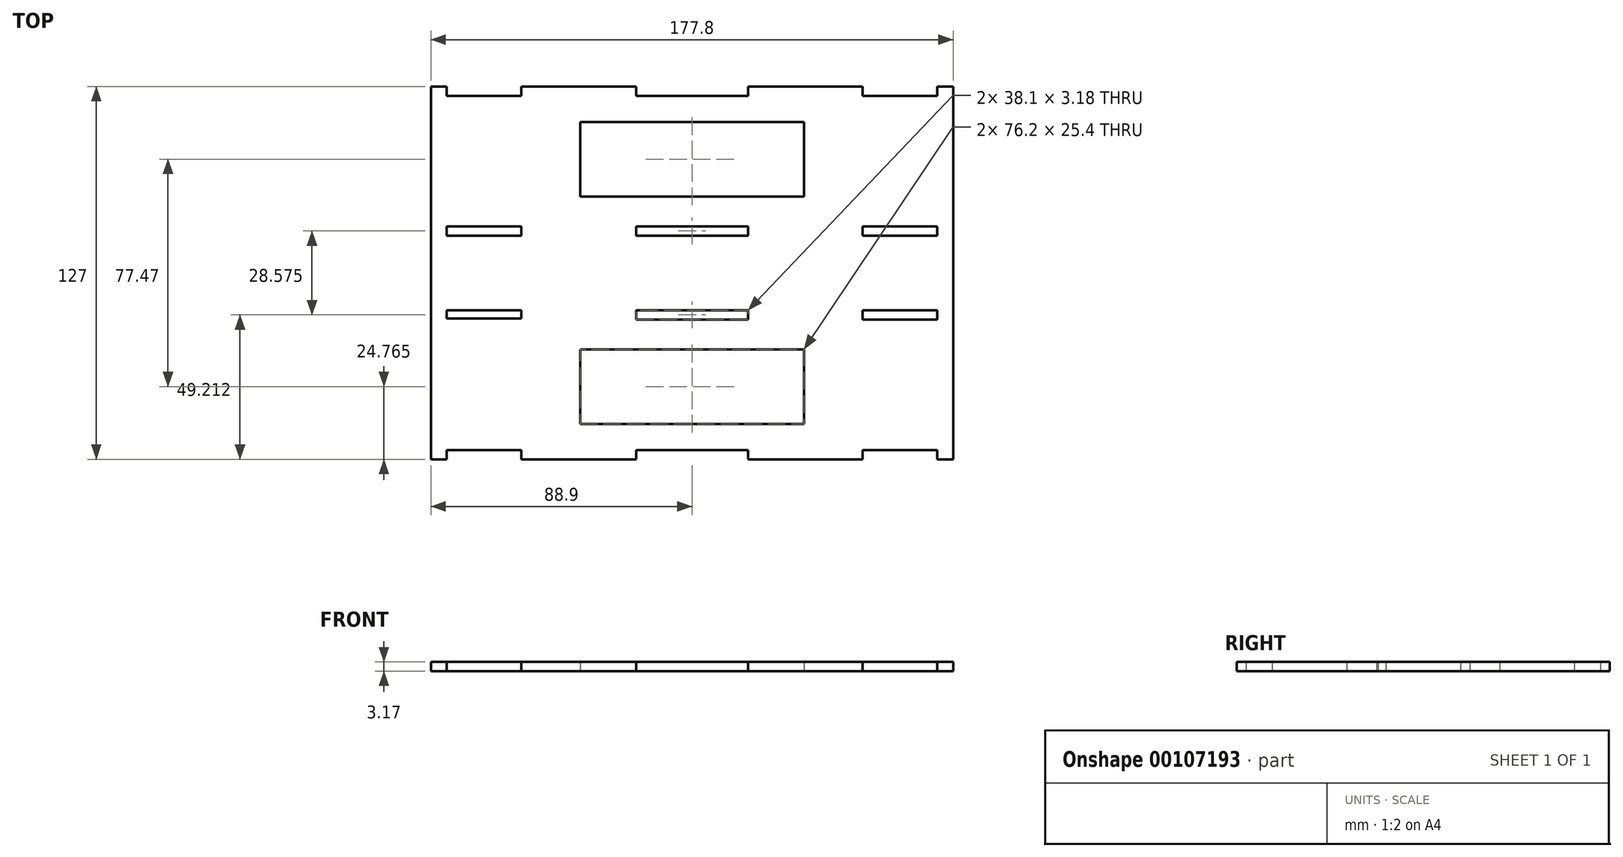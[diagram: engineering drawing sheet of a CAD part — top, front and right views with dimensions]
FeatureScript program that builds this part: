
annotation { "Feature Type Name" : "Feature", "Feature Type Description" : "" }
export const myFeature = defineFeature(function(context is Context, id is Id, definition is map)
    precondition{}
    {
        {
            var Q0;
            Q0=qCreatedBy(makeId("Top.planeOp"),FACE);
            var sketch = newSketch(context, id + "F0", { "sketchPlane" : qUnion([Q0])});
            skPoint(sketch, "E0.middle", {"position": v(0, 0) * mm});
            skPoint(sketch, "E1", {"position": v(-76.2, 0) * mm});
            skPoint(sketch, "E2", {"position": v(101.6, 0) * mm});
            skLineSegment(sketch, "E3", {"start": v(-76.2, 63.5) * mm, "end": v(-76.2, -63.5) * mm});
            skLineSegment(sketch, "E4.bottom", {"start": v(-76.2, 63.5) * mm, "end": v(-70.75, 63.5) * mm});
            skLineSegment(sketch, "E4.right", {"start": v(101.6, 63.5) * mm, "end": v(101.6, -63.5) * mm});
            skPoint(sketch, "E5", {"position": v(12.7, 76.2) * mm});
            skPoint(sketch, "E6", {"position": v(12.7, 63.5) * mm});
            skLineSegment(sketch, "E7.MirrorCS", {"start": v(70.75, 63.5) * mm, "end": v(70.75, 60.32) * mm});
            skLineSegment(sketch, "E8.MirrorCS", {"start": v(31.75, 60.32) * mm, "end": v(-6.35, 60.32) * mm});
            skLineSegment(sketch, "E9.MirrorCS", {"start": v(-70.75, 60.32) * mm, "end": v(-45.35, 60.32) * mm});
            skLineSegment(sketch, "E10.MirrorCS", {"start": v(-6.35, 63.5) * mm, "end": v(-6.35, 60.32) * mm});
            skLineSegment(sketch, "E11.MirrorCS", {"start": v(-70.75, 63.5) * mm, "end": v(-70.75, 60.32) * mm});
            skLineSegment(sketch, "E12.MirrorCS", {"start": v(96.15, 63.5) * mm, "end": v(96.15, 60.32) * mm});
            skLineSegment(sketch, "E13.MirrorCS", {"start": v(96.15, 60.32) * mm, "end": v(70.75, 60.32) * mm});
            skLineSegment(sketch, "E14.MirrorCS", {"start": v(31.75, 63.5) * mm, "end": v(31.75, 60.32) * mm});
            skLineSegment(sketch, "E15.MirrorCS", {"start": v(-45.35, 63.5) * mm, "end": v(-45.35, 60.32) * mm});
            skLineSegment(sketch, "E16.trimOffspring", {"start": v(-45.35, 63.5) * mm, "end": v(-6.35, 63.5) * mm});
            skLineSegment(sketch, "E17.trimOffspring", {"start": v(31.75, 63.5) * mm, "end": v(70.75, 63.5) * mm});
            skLineSegment(sketch, "E18.trimOffspring", {"start": v(96.15, 63.5) * mm, "end": v(101.6, 63.5) * mm});
            skPoint(sketch, "E19", {"position": v(90.87, -11.07) * mm});
            skLineSegment(sketch, "E20.MirrorCS", {"start": v(70.75, -12.7) * mm, "end": v(70.75, -15.88) * mm});
            skLineSegment(sketch, "E21.MirrorCS", {"start": v(31.75, -15.88) * mm, "end": v(-6.35, -15.88) * mm});
            skLineSegment(sketch, "E22.MirrorCS", {"start": v(-70.75, -12.7) * mm, "end": v(-45.35, -12.7) * mm});
            skLineSegment(sketch, "E23.MirrorCS", {"start": v(-6.35, -12.7) * mm, "end": v(-6.35, -15.88) * mm});
            skLineSegment(sketch, "E24.MirrorCS", {"start": v(-70.75, -12.7) * mm, "end": v(-70.75, -15.47) * mm});
            skLineSegment(sketch, "E25.MirrorCS", {"start": v(96.15, -12.7) * mm, "end": v(96.15, -15.88) * mm});
            skLineSegment(sketch, "E26.MirrorCS", {"start": v(96.15, -15.88) * mm, "end": v(70.75, -15.88) * mm});
            skLineSegment(sketch, "E27.MirrorCS", {"start": v(31.75, -12.7) * mm, "end": v(31.75, -15.88) * mm});
            skLineSegment(sketch, "E28.MirrorCS", {"start": v(-45.35, -12.7) * mm, "end": v(-45.35, -15.47) * mm});
            skLineSegment(sketch, "E29", {"start": v(96.15, -12.7) * mm, "end": v(70.75, -12.7) * mm});
            skLineSegment(sketch, "E30", {"start": v(31.75, -12.7) * mm, "end": v(-6.35, -12.7) * mm});
            skLineSegment(sketch, "E31", {"start": v(-45.35, -15.47) * mm, "end": v(-70.75, -15.47) * mm});
            skLineSegment(sketch, "E32.MirrorCS", {"start": v(96.15, 12.7) * mm, "end": v(96.15, 15.87) * mm});
            skLineSegment(sketch, "E33.MirrorCS", {"start": v(70.75, 12.7) * mm, "end": v(70.75, 15.87) * mm});
            skLineSegment(sketch, "E34.MirrorCS", {"start": v(-6.35, 12.7) * mm, "end": v(-6.35, 15.87) * mm});
            skLineSegment(sketch, "E35.MirrorCS", {"start": v(-70.75, 12.7) * mm, "end": v(-70.75, 15.87) * mm});
            skLineSegment(sketch, "E36.MirrorCS", {"start": v(-45.35, 12.7) * mm, "end": v(-45.35, 15.87) * mm});
            skLineSegment(sketch, "E37.MirrorCS", {"start": v(31.75, 12.7) * mm, "end": v(31.75, 15.87) * mm});
            skLineSegment(sketch, "E38.MirrorCS", {"start": v(-70.75, 15.87) * mm, "end": v(-45.35, 15.87) * mm});
            skLineSegment(sketch, "E39.MirrorCS", {"start": v(31.75, 15.87) * mm, "end": v(-6.35, 15.87) * mm});
            skLineSegment(sketch, "E40.MirrorCS", {"start": v(96.15, 12.7) * mm, "end": v(70.75, 12.7) * mm});
            skLineSegment(sketch, "E41.MirrorCS", {"start": v(-45.35, 12.7) * mm, "end": v(-70.75, 12.7) * mm});
            skLineSegment(sketch, "E42.MirrorCS", {"start": v(96.15, 15.87) * mm, "end": v(70.75, 15.87) * mm});
            skLineSegment(sketch, "E43.MirrorCS", {"start": v(31.75, 12.7) * mm, "end": v(-6.35, 12.7) * mm});
            skLineSegment(sketch, "E44.MirrorCS", {"start": v(-70.75, -63.5) * mm, "end": v(-70.75, -60.32) * mm});
            skLineSegment(sketch, "E45.MirrorCS", {"start": v(-76.2, -63.5) * mm, "end": v(-70.75, -63.5) * mm});
            skLineSegment(sketch, "E46.MirrorCS", {"start": v(-6.35, -63.5) * mm, "end": v(-6.35, -60.32) * mm});
            skLineSegment(sketch, "E47.MirrorCS", {"start": v(96.15, -63.5) * mm, "end": v(96.15, -60.32) * mm});
            skLineSegment(sketch, "E48.MirrorCS", {"start": v(31.75, -63.5) * mm, "end": v(31.75, -60.32) * mm});
            skLineSegment(sketch, "E49.MirrorCS", {"start": v(70.75, -63.5) * mm, "end": v(70.75, -60.32) * mm});
            skLineSegment(sketch, "E50.MirrorCS", {"start": v(96.15, -63.5) * mm, "end": v(101.6, -63.5) * mm});
            skLineSegment(sketch, "E51.MirrorCS", {"start": v(-45.35, -63.5) * mm, "end": v(-45.35, -60.32) * mm});
            skPoint(sketch, "E52.MirrorP", {"position": v(12.7, -76.2) * mm});
            skLineSegment(sketch, "E53.MirrorCS", {"start": v(31.75, -63.5) * mm, "end": v(70.75, -63.5) * mm});
            skPoint(sketch, "E54.MirrorP", {"position": v(12.7, -63.5) * mm});
            skLineSegment(sketch, "E55.MirrorCS", {"start": v(-45.35, -63.5) * mm, "end": v(-6.35, -63.5) * mm});
            skLineSegment(sketch, "E56.MirrorCS", {"start": v(-70.75, -60.32) * mm, "end": v(-45.35, -60.32) * mm});
            skLineSegment(sketch, "E57.MirrorCS", {"start": v(96.15, -60.32) * mm, "end": v(70.75, -60.32) * mm});
            skLineSegment(sketch, "E58.MirrorCS", {"start": v(31.75, -60.32) * mm, "end": v(-6.35, -60.32) * mm});
            skLineSegment(sketch, "E59.bottom", {"start": v(-25.4, -26.04) * mm, "end": v(50.8, -26.04) * mm});
            skLineSegment(sketch, "E59.top", {"start": v(-25.4, -51.44) * mm, "end": v(50.8, -51.44) * mm});
            skLineSegment(sketch, "E59.left", {"start": v(-25.4, -26.04) * mm, "end": v(-25.4, -51.44) * mm});
            skLineSegment(sketch, "E59.right", {"start": v(50.8, -26.04) * mm, "end": v(50.8, -51.44) * mm});
            skLineSegment(sketch, "E60.MirrorCS", {"start": v(-25.4, 26.04) * mm, "end": v(50.8, 26.04) * mm});
            skLineSegment(sketch, "E61.MirrorCS", {"start": v(-25.4, 26.04) * mm, "end": v(-25.4, 51.44) * mm});
            skLineSegment(sketch, "E62.MirrorCS", {"start": v(-25.4, 51.44) * mm, "end": v(50.8, 51.44) * mm});
            skLineSegment(sketch, "E63.MirrorCS", {"start": v(50.8, 26.04) * mm, "end": v(50.8, 51.44) * mm});
            skSolve(sketch);
        }
        {
            var Q0;
            Q0=makeQuery(id+"F0.imprint","IMPRINT",FACE,{"disambiguationData":[TD([[makeQuery(id+"F0.imprint","IMPRINT",EDGE,{"derivedFrom":sQuery(id+"F0.wireOp",EDGE,"E4.bottom")}),-1.0]])]});
            extrude(context, id + "F1", {"entities" : qUnion([Q0]), "depth" : 3.17 * mm});
        }
    });
